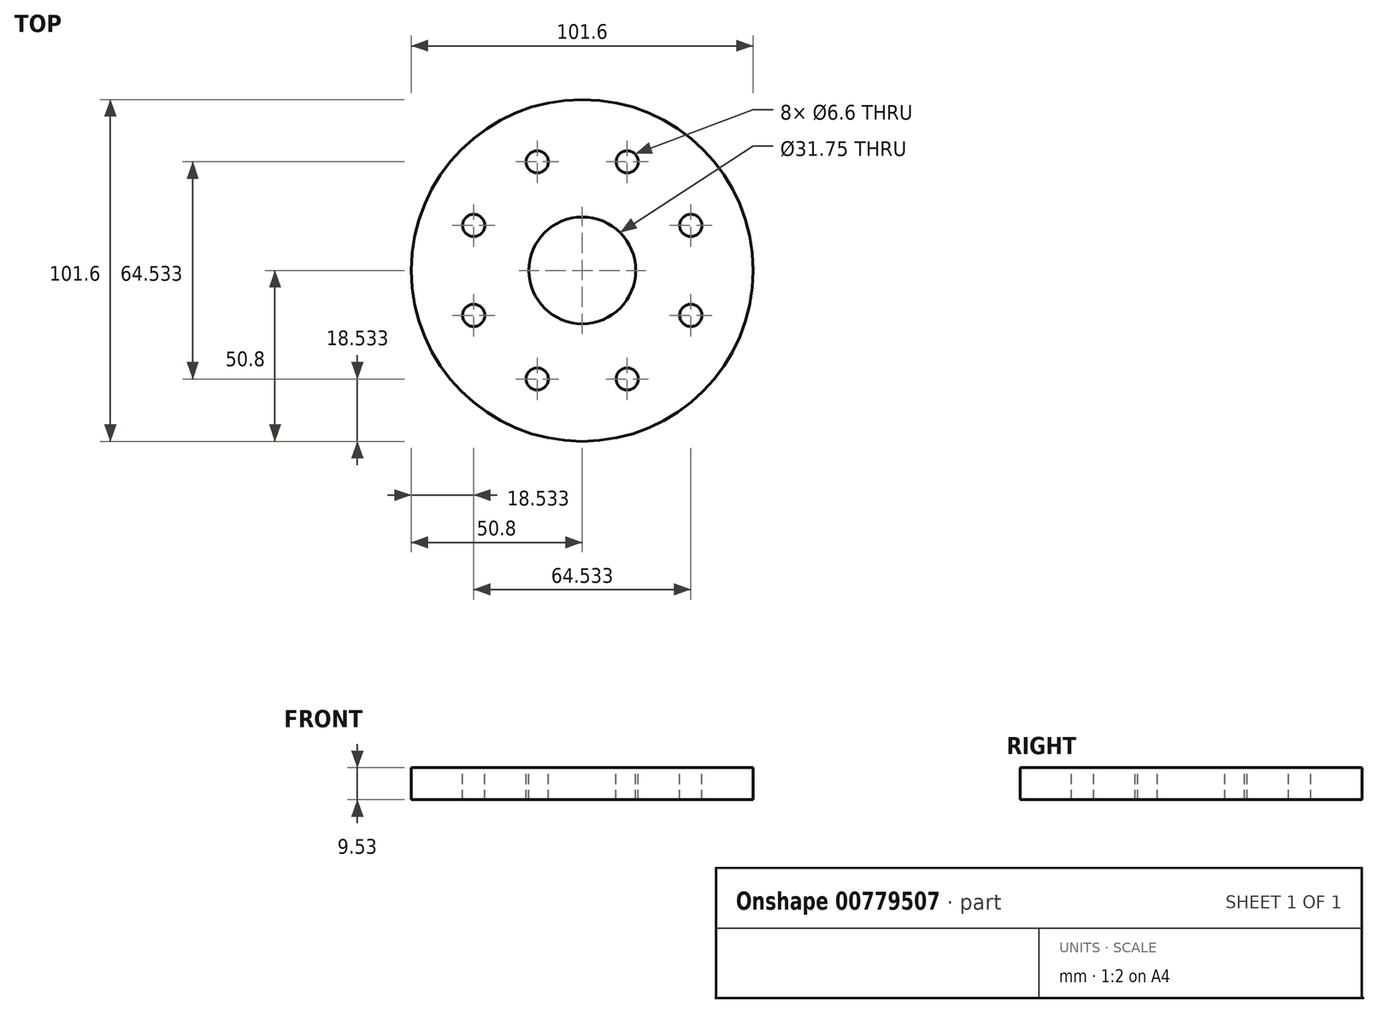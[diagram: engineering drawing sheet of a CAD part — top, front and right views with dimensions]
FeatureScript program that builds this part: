
annotation { "Feature Type Name" : "Feature", "Feature Type Description" : "" }
export const myFeature = defineFeature(function(context is Context, id is Id, definition is map)
    precondition{}
    {
        {
            var Q0;
            Q0=qCreatedBy(makeId("Top.planeOp"),FACE);
            var sketch = newSketch(context, id + "F0", { "sketchPlane" : qUnion([Q0])});
            skCircle(sketch, "E0", {"center": v(0, 0) * mm, "radius": 50.8 * mm});
            skSolve(sketch);
        }
        {
            var Q0;
            Q0=makeQuery(id+"F0.imprint","IMPRINT",FACE,{"disambiguationData":[TD([[makeQuery(id+"F0.imprint","IMPRINT",EDGE,{"derivedFrom":sQuery(id+"F0.wireOp",EDGE,"E0")}),1.0]])]});
            extrude(context, id + "F1", {"entities" : qUnion([Q0]), "depth" : 9.52 * mm, "offsetDistance" : 25.4 * mm});
        }
        {
            var Q0;
            Q0=makeQuery(id+"F1.opExtrude","CAP_FACE",FACE,{"disambiguationData":[OSD([sQuery(id+"F0.wireOp",EDGE,"E0")])],"isStart":false});
            var sketch = newSketch(context, id + "F2", { "sketchPlane" : qUnion([Q0])});
            skCircle(sketch, "E1", {"center": v(0, 0) * mm, "radius": 15.88 * mm});
            skSolve(sketch);
        }
        {
            var Q0;
            Q0=makeQuery(id+"F2.imprint","IMPRINT",FACE,{"disambiguationData":[TD([[makeQuery(id+"F2.imprint","IMPRINT",EDGE,{"derivedFrom":sQuery(id+"F2.wireOp",EDGE,"E1")}),1.0]])]});
            extrude(context, id + "F3", {"entities" : qUnion([Q0]), "operationType" : NewBodyOperationType.REMOVE, "endBound" : BoundingType.THROUGH_ALL, "oppositeDirection" : true, "depth" : 25.4 * mm, "offsetDistance" : 25.4 * mm});
        }
        {
            var Q0;
            Q0=makeQuery(id+"F1.opExtrude","CAP_FACE",FACE,{"disambiguationData":[OSD([sQuery(id+"F0.wireOp",EDGE,"E0")])],"isStart":false});
            var sketch = newSketch(context, id + "F4", { "sketchPlane" : qUnion([Q0])});
            skPoint(sketch, "E2", {"position": v(-32.27, -13.37) * mm});
            skPoint(sketch, "E3.1.0", {"position": v(-13.37, -32.27) * mm});
            skPoint(sketch, "E3.2.0", {"position": v(13.37, -32.27) * mm});
            skPoint(sketch, "E3.3.0", {"position": v(32.27, -13.37) * mm});
            skPoint(sketch, "E3.4.0", {"position": v(32.27, 13.37) * mm});
            skPoint(sketch, "E3.5.0", {"position": v(13.37, 32.27) * mm});
            skPoint(sketch, "E3.6.0", {"position": v(-13.37, 32.27) * mm});
            skPoint(sketch, "E3.7.0", {"position": v(-32.27, 13.37) * mm});
            skPoint(sketch, "E3.center", {"position": v(0, 0) * mm});
            skSolve(sketch);
        }
        {
            var Q0;
            Q0=sQuery(id+"F4.wireOp",VERTEX,"E3.6.0");
            var Q1;
            Q1=sQuery(id+"F4.wireOp",VERTEX,"E3.7.0");
            var Q2;
            Q2=sQuery(id+"F4.wireOp",VERTEX,"E2");
            var Q3;
            Q3=sQuery(id+"F4.wireOp",VERTEX,"E3.1.0");
            var Q4;
            Q4=sQuery(id+"F4.wireOp",VERTEX,"E3.2.0");
            var Q5;
            Q5=sQuery(id+"F4.wireOp",VERTEX,"E3.3.0");
            var Q6;
            Q6=sQuery(id+"F4.wireOp",VERTEX,"E3.4.0");
            var Q7;
            Q7=sQuery(id+"F4.wireOp",VERTEX,"E3.5.0");
            var Q8;
            Q8=makeQuery(id+"F1.opExtrude","SWEPT_BODY",BODY,{"disambiguationData":[OSD([sQuery(id+"F0.wireOp",EDGE,"E0")])]});
            hole(context, id + "F5", {"style" : HoleStyle.SIMPLE, "endStyle" : HoleEndStyle.THROUGH, "standardTappedOrClearance" : lookupTablePath({ "standard" : "ISO", "fit" : "Normal", "size" : "M6", "type" : "Clearance" }), "standardBlindInLast" : lookupTablePath({ "fit" : "Standard", "standard" : "ISO", "size" : "M6", "type" : "Clearance" }), "holeDiameter" : 6.6 * mm, "majorDiameter" : 6 * mm, "isTappedThrough" : true, "tappedDepth" : 3.63 * mm, "tapClearance" : 3, "startFromSketch" : true, "locations" : qUnion([Q0, Q1, Q2, Q3, Q4, Q5, Q6, Q7]), "scope" : qUnion([Q8])});
        }
        {
            var Q0;
            Q0=makeQuery(id+"F1.opExtrude","CAP_FACE",FACE,{"disambiguationData":[OSD([sQuery(id+"F0.wireOp",EDGE,"E0")])],"isStart":false});
            var sketch = newSketch(context, id + "F6", { "sketchPlane" : qUnion([Q0])});
            skLineSegment(sketch, "E4.bottom", {"start": v(0, 88.49) * mm, "end": v(92, 88.49) * mm});
            skLineSegment(sketch, "E4.top", {"start": v(0, -93.4) * mm, "end": v(92, -93.4) * mm});
            skLineSegment(sketch, "E4.left", {"start": v(0, 88.49) * mm, "end": v(0, -93.4) * mm});
            skLineSegment(sketch, "E4.right", {"start": v(92, 88.49) * mm, "end": v(92, -93.4) * mm});
            skSolve(sketch);
        }
        {
            var Q0;
            {var subQ1=sQuery(id+"F6.wireOp",EDGE,"E4.bottom");Q0=makeQuery(id+"F6.imprint","IMPRINT",FACE,{"disambiguationData":[TD([[makeQuery(id+"F6.imprint","IMPRINT",EDGE,{"derivedFrom":subQ1}),-1.0]])]});}
            var Q1;
            Q1=makeQuery(id+"F6.imprint","IMPRINT",FACE,{"disambiguationData":[TD([[makeQuery(id+"F6.imprint","IMPRINT",EDGE,{"derivedFrom":makeQuery(id+"F5.hole-4.boolean.opBoolean","COPY",EDGE,{"derivedFrom":makeQuery(id+"F5.hole-4.opRevolve","SWEPT_EDGE",EDGE,{"disambiguationData":[OSD([sQuery(id+"F5.hole-4.sketch.wireOp",EDGE,"core_line_2"),sQuery(id+"F5.hole-4.sketch.wireOp",EDGE,"core_line_3")])]})})}),-1.0]])]});
            extrude(context, id + "F7", {"entities" : qUnion([Q0, Q1]), "operationType" : NewBodyOperationType.REMOVE, "endBound" : BoundingType.THROUGH_ALL, "oppositeDirection" : true, "depth" : 25.4 * mm, "offsetDistance" : 25.4 * mm});
        }
    });
